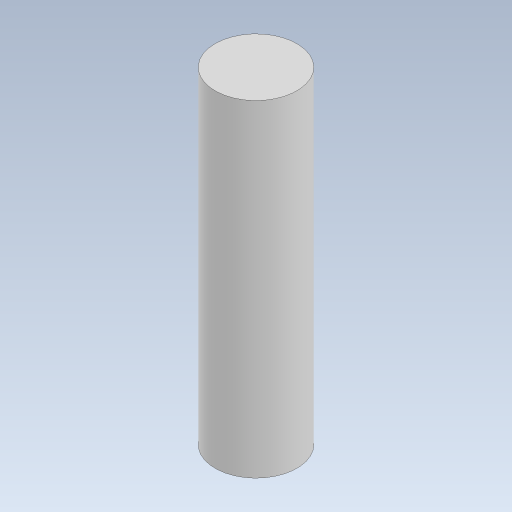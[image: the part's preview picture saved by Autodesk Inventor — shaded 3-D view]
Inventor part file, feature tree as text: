
AUTODESK INVENTOR PART (.ipt)
format: ipt  version: 2023 (Build 270158000, 158)  size: 76,800 bytes
history: native  units: in
note: dims shown in document units (in); Inventor stores cm internally (conversion verified against a paired STEP export)
features: extrude x1, sketch x1
ambient origin geometry x8: Origin, YZ Plane, XZ Plane, XY Plane, X Axis, Y Axis, Z Axis, Center Point
bodies: Solid1 (feature_tree)
feature tree (2):
  extrude  "Extrusion1"  Depth=1.0in TaperAngle=0.0deg
  sketch  "Sketch1"  dims[d0=0.25in d1=1.0in d2=0.0in]
